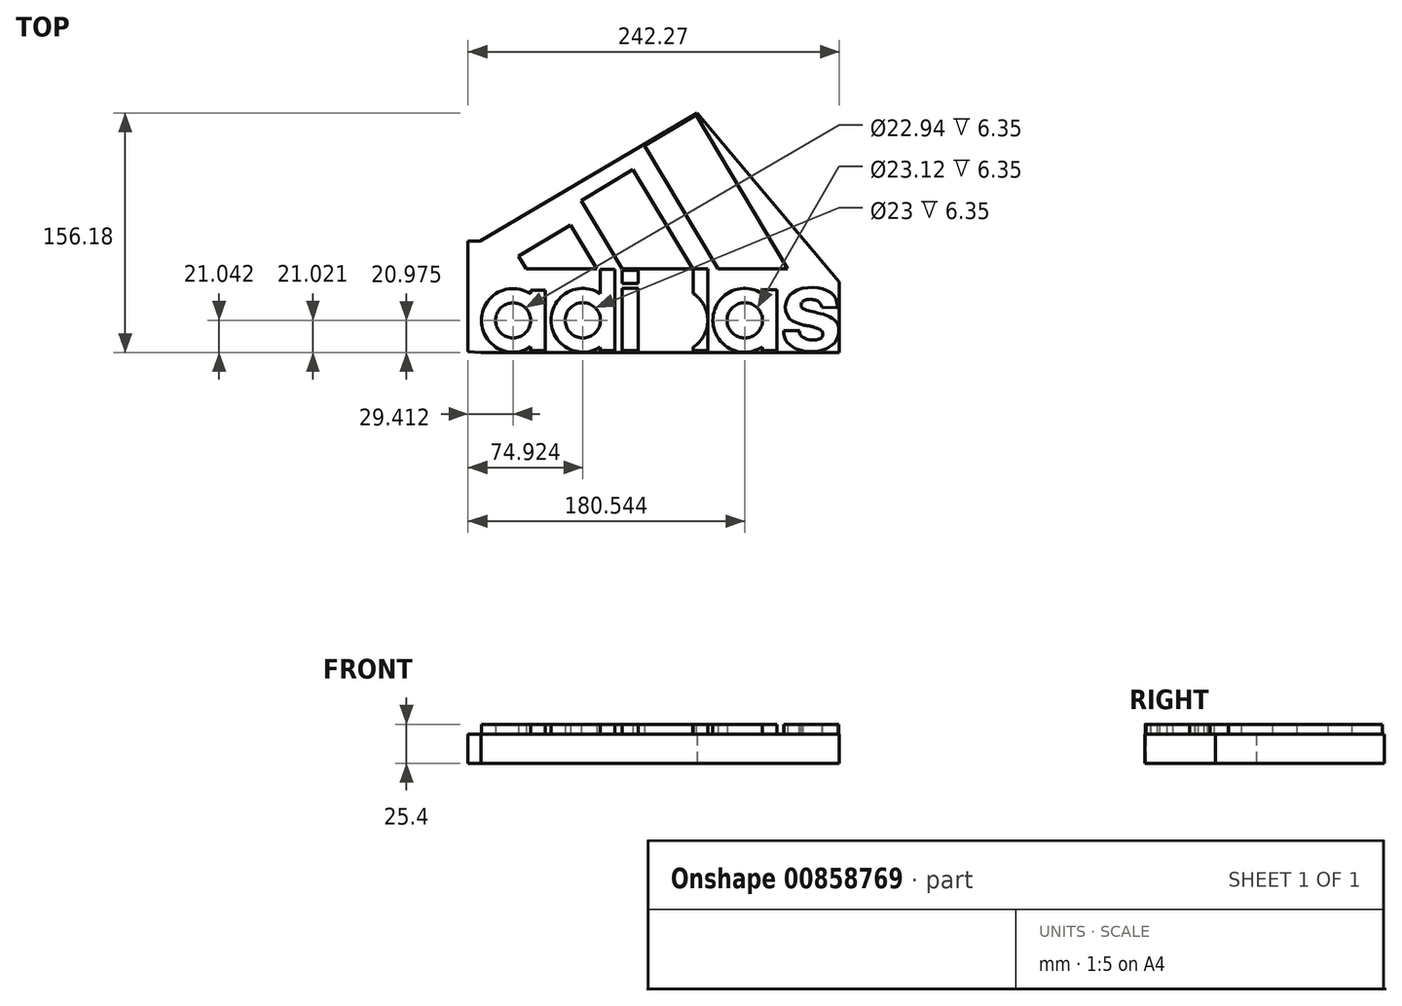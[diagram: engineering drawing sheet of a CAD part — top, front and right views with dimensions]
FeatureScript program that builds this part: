
annotation { "Feature Type Name" : "Feature", "Feature Type Description" : "" }
export const myFeature = defineFeature(function(context is Context, id is Id, definition is map)
    precondition{}
    {
        {
            var Q0;
            Q0=qCreatedBy(makeId("Top.planeOp"),FACE);
            var sketch = newSketch(context, id + "F0", { "sketchPlane" : qUnion([Q0])});
            skLineSegment(sketch, "E0", {"start": v(-91.26, -15.7) * mm, "end": v(-57.48, 4.7) * mm});
            skLineSegment(sketch, "E1", {"start": v(-57.48, 4.7) * mm, "end": v(-40.16, -23.99) * mm});
            skLineSegment(sketch, "E2", {"start": v(-40.16, -23.99) * mm, "end": v(-86.26, -23.99) * mm});
            skLineSegment(sketch, "E3", {"start": v(-86.26, -23.99) * mm, "end": v(-91.26, -15.7) * mm});
            skLineSegment(sketch, "E4", {"start": v(-16.65, 40.75) * mm, "end": v(-50.43, 20.37) * mm});
            skLineSegment(sketch, "E5", {"start": v(-50.43, 20.37) * mm, "end": v(-23.6, -24.1) * mm});
            skLineSegment(sketch, "E6", {"start": v(-23.6, -24.1) * mm, "end": v(22.26, -24.1) * mm});
            skLineSegment(sketch, "E7", {"start": v(22.26, -24.1) * mm, "end": v(-16.65, 40.75) * mm});
            skLineSegment(sketch, "E8", {"start": v(-9.03, 56.5) * mm, "end": v(24.5, 76.51) * mm});
            skLineSegment(sketch, "E9", {"start": v(24.5, 76.51) * mm, "end": v(84.33, -23.8) * mm});
            skLineSegment(sketch, "E10", {"start": v(84.33, -23.8) * mm, "end": v(38.86, -23.8) * mm});
            skLineSegment(sketch, "E11", {"start": v(38.86, -23.8) * mm, "end": v(-9.03, 56.5) * mm});
            skLineSegment(sketch, "E12", {"start": v(-73.9, -37.96) * mm, "end": v(-73.9, -77.28) * mm});
            skLineSegment(sketch, "E13", {"start": v(-73.9, -77.28) * mm, "end": v(-83.4, -77.28) * mm});
            skLineSegment(sketch, "E14", {"start": v(-83.4, -77.28) * mm, "end": v(-83.4, -75.06) * mm});
            skLineSegment(sketch, "E15", {"start": v(-73.9, -37.96) * mm, "end": v(-83.49, -37.96) * mm});
            skLineSegment(sketch, "E16", {"start": v(-83.49, -37.96) * mm, "end": v(-83.49, -39.74) * mm});
            skCircle(sketch, "E17", {"center": v(-94.85, -57.58) * mm, "radius": 11.47 * mm});
            skCircle(sketch, "E18", {"center": v(-94.85, -57.58) * mm, "radius": 20.72 * mm});
            skCircle(sketch, "E19", {"center": v(-49.34, -57.5) * mm, "radius": 11.5 * mm});
            skCircle(sketch, "E20", {"center": v(-49.34, -57.5) * mm, "radius": 20.77 * mm});
            skLineSegment(sketch, "E21", {"start": v(-83.4, -75.06) * mm, "end": v(-83.49, -39.74) * mm});
            skLineSegment(sketch, "E22.bottom", {"start": v(-38.01, -24.27) * mm, "end": v(-28.56, -24.27) * mm});
            skLineSegment(sketch, "E22.top", {"start": v(-38.01, -77.35) * mm, "end": v(-28.56, -77.35) * mm});
            skLineSegment(sketch, "E22.left", {"start": v(-38.01, -24.27) * mm, "end": v(-38.01, -77.35) * mm});
            skLineSegment(sketch, "E22.right", {"start": v(-28.56, -24.27) * mm, "end": v(-28.56, -77.35) * mm});
            skLineSegment(sketch, "E23.bottom", {"start": v(-23.6, -33.52) * mm, "end": v(-13.2, -33.52) * mm});
            skLineSegment(sketch, "E23.top", {"start": v(-23.6, -24.9) * mm, "end": v(-13.2, -24.9) * mm});
            skLineSegment(sketch, "E23.left", {"start": v(-23.6, -33.52) * mm, "end": v(-23.6, -24.9) * mm});
            skLineSegment(sketch, "E23.right", {"start": v(-13.2, -33.52) * mm, "end": v(-13.2, -24.9) * mm});
            skLineSegment(sketch, "E24.bottom", {"start": v(-23.68, -36.53) * mm, "end": v(-13.2, -36.53) * mm});
            skLineSegment(sketch, "E24.top", {"start": v(-23.68, -77.24) * mm, "end": v(-13.2, -77.24) * mm});
            skLineSegment(sketch, "E24.left", {"start": v(-23.68, -36.53) * mm, "end": v(-23.68, -77.24) * mm});
            skLineSegment(sketch, "E24.right", {"start": v(-13.2, -36.53) * mm, "end": v(-13.2, -77.24) * mm});
            skLineSegment(sketch, "E25.bottom", {"start": v(32.16, -77.24) * mm, "end": v(22.7, -77.24) * mm});
            skLineSegment(sketch, "E25.top", {"start": v(32.16, -24.1) * mm, "end": v(22.7, -24.1) * mm});
            skLineSegment(sketch, "E25.left", {"start": v(32.16, -77.24) * mm, "end": v(32.16, -24.1) * mm});
            skLineSegment(sketch, "E25.right", {"start": v(22.7, -77.24) * mm, "end": v(22.7, -24.1) * mm});
            skCircle(sketch, "E26", {"center": v(11.42, -57.53) * mm, "radius": 11.42 * mm});
            skCircle(sketch, "E27", {"center": v(11.42, -57.53) * mm, "radius": 20.73 * mm});
            skCircle(sketch, "E28", {"center": v(56.28, -57.53) * mm, "radius": 11.56 * mm});
            skFitSpline(sketch, "E29", {"points": [v(81.61, -64.38) * mm, v(117.73, -63.94) * mm], "startDerivative": vector(-1.77, -53.7) * mm, "endDerivative": vector(-0.99, 57.2) * mm});
            skFitSpline(sketch, "E30", {"points": [v(117.73, -63.94) * mm, v(93.06, -47.23) * mm], "startDerivative": vector(-0.33, 41.67) * mm, "endDerivative": vector(4.32, 20.27) * mm});
            skLineSegment(sketch, "E31.bottom", {"start": v(67.63, -37.71) * mm, "end": v(77.36, -37.71) * mm});
            skLineSegment(sketch, "E31.top", {"start": v(67.63, -77.26) * mm, "end": v(77.36, -77.26) * mm});
            skLineSegment(sketch, "E31.left", {"start": v(67.63, -37.71) * mm, "end": v(67.63, -77.26) * mm});
            skLineSegment(sketch, "E31.right", {"start": v(77.36, -37.71) * mm, "end": v(77.36, -77.26) * mm});
            skCircle(sketch, "E32", {"center": v(56.28, -57.53) * mm, "radius": 20.8 * mm});
            skFitSpline(sketch, "E33", {"points": [v(93.06, -47.23) * mm, v(106.38, -49.16) * mm], "startDerivative": vector(3.38, 16.63) * mm, "endDerivative": vector(-1.1, -17.88) * mm});
            skLineSegment(sketch, "E34", {"start": v(92.14, -64.35) * mm, "end": v(81.61, -64.38) * mm});
            skLineSegment(sketch, "E35", {"start": v(116.62, -49.23) * mm, "end": v(106.38, -49.16) * mm});
            skPoint(sketch, "E36.1.internal.snap0", {"position": v(111.5, -49.2) * mm});
            skFitSpline(sketch, "E37", {"points": [v(92.14, -64.35) * mm, v(106.58, -64.35) * mm], "startDerivative": vector(-5.97, -20.58) * mm, "endDerivative": vector(-12.92, 27.57) * mm});
            skFitSpline(sketch, "E38", {"points": [v(106.58, -64.35) * mm, v(94, -60.6) * mm], "startDerivative": vector(-5.75, 4.6) * mm, "endDerivative": vector(-16.11, 1.37) * mm});
            skFitSpline(sketch, "E39", {"points": [v(94, -60.6) * mm, v(87.01, -57.76) * mm, v(84.52, -55.12) * mm, v(82.67, -49.71) * mm, v(83.67, -44.8) * mm, v(85.52, -41.38) * mm, v(89.93, -38.03) * mm, v(97.55, -36.18) * mm, v(104.32, -36.54) * mm, v(110.16, -38.25) * mm, v(114.15, -41.3) * mm, v(115.93, -44.37) * mm, v(116.64, -48.36) * mm, v(116.71, -49.23) * mm, v(116.62, -49.23) * mm], "startDerivative": vector(-85.4, 29.14) * mm, "endDerivative": vector(-29.4, 5.26) * mm});
            skSolve(sketch);
        }
        {
            var Q0;
            Q0=qCreatedBy(makeId("Top.planeOp"),FACE);
            var sketch = newSketch(context, id + "F1", { "sketchPlane" : qUnion([Q0])});
            skLineSegment(sketch, "E40", {"start": v(118, -70.14) * mm, "end": v(16.35, 70.24) * mm});
            skLineSegment(sketch, "E41", {"start": v(16.35, 70.24) * mm, "end": v(-115.79, -59.54) * mm});
            skLineSegment(sketch, "E42", {"start": v(-115.79, -59.54) * mm, "end": v(118, -70.14) * mm});
            skLineSegment(sketch, "E43", {"start": v(-115.79, -59.54) * mm, "end": v(-115.79, -78.55) * mm});
            skLineSegment(sketch, "E44", {"start": v(-115.79, -78.55) * mm, "end": v(118, -78.55) * mm});
            skLineSegment(sketch, "E45", {"start": v(118, -78.55) * mm, "end": v(118, -70.14) * mm});
            skLineSegment(sketch, "E46", {"start": v(118, -70.14) * mm, "end": v(118, -32.43) * mm});
            skLineSegment(sketch, "E47", {"start": v(118, -32.43) * mm, "end": v(25.04, 77.63) * mm});
            skLineSegment(sketch, "E48", {"start": v(25.04, 77.63) * mm, "end": v(-116.56, -5.85) * mm});
            skLineSegment(sketch, "E49", {"start": v(-116.56, -5.85) * mm, "end": v(-115.79, -59.54) * mm});
            skLineSegment(sketch, "E50", {"start": v(-116.56, -5.85) * mm, "end": v(-124.26, -5.96) * mm});
            skLineSegment(sketch, "E51", {"start": v(-124.26, -5.96) * mm, "end": v(-124.26, -77.9) * mm});
            skLineSegment(sketch, "E52", {"start": v(-124.26, -77.9) * mm, "end": v(-115.79, -78.55) * mm});
            skSolve(sketch);
        }
        {
            var Q0;
            Q0=makeQuery(id+"F0.imprint","IMPRINT",FACE,{"disambiguationData":[TD([[makeQuery(id+"F0.imprint","IMPRINT",EDGE,{"derivedFrom":sQuery(id+"F0.wireOp",EDGE,"E4")}),1.0]])]});
            var Q1;
            Q1=makeQuery(id+"F0.imprint","IMPRINT",FACE,{"disambiguationData":[TD([[makeQuery(id+"F0.imprint","IMPRINT",EDGE,{"derivedFrom":sQuery(id+"F0.wireOp",EDGE,"E8")}),-1.0]])]});
            var Q2;
            Q2=makeQuery(id+"F0.imprint","IMPRINT",FACE,{"disambiguationData":[TD([[makeQuery(id+"F0.imprint","IMPRINT",EDGE,{"derivedFrom":sQuery(id+"F0.wireOp",EDGE,"E0")}),-1.0]])]});
            var Q3;
            {var subQ0=sQuery(id+"F0.wireOp",EDGE,"E22.left");var subQ1=sQuery(id+"F0.wireOp",EDGE,"E19");var subQ2=makeQuery(id+"F0.imprint","INTERSECT",VERTEX,{"disambiguationData":[OD(0.0)],"derivedFrom":[subQ1,subQ0]});Q3=makeQuery(id+"F0.imprint","IMPRINT",FACE,{"disambiguationData":[TD([[makeQuery(id+"F0.imprint","IMPRINT",EDGE,{"disambiguationData":[TD([[subQ2,-1.0]])],"derivedFrom":subQ1}),-1.0]])]});}
            var Q4;
            {var subQ0=sQuery(id+"F0.wireOp",EDGE,"E22.left");var subQ1=sQuery(id+"F0.wireOp",EDGE,"E19");var subQ2=makeQuery(id+"F0.imprint","INTERSECT",VERTEX,{"disambiguationData":[OD(0.0)],"derivedFrom":[subQ1,subQ0]});Q4=makeQuery(id+"F0.imprint","IMPRINT",FACE,{"disambiguationData":[TD([[makeQuery(id+"F0.imprint","IMPRINT",EDGE,{"disambiguationData":[TD([[subQ2,1.0]])],"derivedFrom":subQ1}),-1.0]])]});}
            var Q5;
            {var subQ1=sQuery(id+"F0.wireOp",EDGE,"E22.bottom");Q5=makeQuery(id+"F0.imprint","IMPRINT",FACE,{"disambiguationData":[TD([[makeQuery(id+"F0.imprint","IMPRINT",EDGE,{"derivedFrom":subQ1}),-1.0]])]});}
            var Q6;
            {var subQ0=sQuery(id+"F0.wireOp",EDGE,"E21");var subQ1=sQuery(id+"F0.wireOp",EDGE,"E17");var subQ2=makeQuery(id+"F0.imprint","INTERSECT",VERTEX,{"disambiguationData":[OD(0.0)],"derivedFrom":[subQ1,subQ0]});Q6=makeQuery(id+"F0.imprint","IMPRINT",FACE,{"disambiguationData":[TD([[makeQuery(id+"F0.imprint","IMPRINT",EDGE,{"disambiguationData":[TD([[subQ2,-1.0]])],"derivedFrom":subQ1}),-1.0]])]});}
            var Q7;
            Q7=makeQuery(id+"F0.imprint","IMPRINT",FACE,{"disambiguationData":[TD([[makeQuery(id+"F0.imprint","IMPRINT",EDGE,{"derivedFrom":sQuery(id+"F0.wireOp",EDGE,"E12")}),-1.0]])]});
            var Q8;
            {var subQ0=sQuery(id+"F0.wireOp",EDGE,"E21");var subQ1=sQuery(id+"F0.wireOp",EDGE,"E17");var subQ2=makeQuery(id+"F0.imprint","INTERSECT",VERTEX,{"disambiguationData":[OD(0.0)],"derivedFrom":[subQ1,subQ0]});Q8=makeQuery(id+"F0.imprint","IMPRINT",FACE,{"disambiguationData":[TD([[makeQuery(id+"F0.imprint","IMPRINT",EDGE,{"disambiguationData":[TD([[subQ2,1.0]])],"derivedFrom":subQ1}),-1.0]])]});}
            var Q9;
            Q9=makeQuery(id+"F0.imprint","IMPRINT",FACE,{"disambiguationData":[TD([[makeQuery(id+"F0.imprint","IMPRINT",EDGE,{"derivedFrom":sQuery(id+"F0.wireOp",EDGE,"E24.bottom")}),-1.0]])]});
            var Q10;
            Q10=makeQuery(id+"F0.imprint","IMPRINT",FACE,{"disambiguationData":[TD([[makeQuery(id+"F0.imprint","IMPRINT",EDGE,{"derivedFrom":sQuery(id+"F0.wireOp",EDGE,"E23.bottom")}),1.0]])]});
            var Q11;
            {var subQ0=sQuery(id+"F0.wireOp",EDGE,"E27");var subQ1=sQuery(id+"F0.wireOp",EDGE,"E25.right");var subQ2=makeQuery(id+"F0.imprint","INTERSECT",VERTEX,{"disambiguationData":[OD(0.0)],"derivedFrom":[subQ1,subQ0]});Q11=makeQuery(id+"F0.imprint","IMPRINT",FACE,{"disambiguationData":[TD([[makeQuery(id+"F0.imprint","IMPRINT",EDGE,{"disambiguationData":[TD([[subQ2,-1.0]])],"derivedFrom":subQ1}),1.0]])]});}
            var Q12;
            {var subQ0=sQuery(id+"F0.wireOp",EDGE,"E27");var subQ1=sQuery(id+"F0.wireOp",EDGE,"E25.right");var subQ2=makeQuery(id+"F0.imprint","INTERSECT",VERTEX,{"disambiguationData":[OD(0.0)],"derivedFrom":[subQ1,subQ0]});Q12=makeQuery(id+"F0.imprint","IMPRINT",FACE,{"disambiguationData":[TD([[makeQuery(id+"F0.imprint","IMPRINT",EDGE,{"disambiguationData":[TD([[subQ2,-1.0]])],"derivedFrom":subQ1}),-1.0]])]});}
            var Q13;
            {var subQ1=sQuery(id+"F0.wireOp",EDGE,"E25.bottom");Q13=makeQuery(id+"F0.imprint","IMPRINT",FACE,{"disambiguationData":[TD([[makeQuery(id+"F0.imprint","IMPRINT",EDGE,{"derivedFrom":subQ1}),-1.0]])]});}
            var Q14;
            {var subQ0=sQuery(id+"F0.wireOp",EDGE,"E31.left");var subQ1=sQuery(id+"F0.wireOp",EDGE,"E28");var subQ2=makeQuery(id+"F0.imprint","INTERSECT",VERTEX,{"disambiguationData":[OD(0.0)],"derivedFrom":[subQ1,subQ0]});Q14=makeQuery(id+"F0.imprint","IMPRINT",FACE,{"disambiguationData":[TD([[makeQuery(id+"F0.imprint","IMPRINT",EDGE,{"disambiguationData":[TD([[subQ2,-1.0]])],"derivedFrom":subQ1}),-1.0]])]});}
            var Q15;
            {var subQ0=sQuery(id+"F0.wireOp",EDGE,"E31.left");var subQ1=sQuery(id+"F0.wireOp",EDGE,"E28");var subQ2=makeQuery(id+"F0.imprint","INTERSECT",VERTEX,{"disambiguationData":[OD(0.0)],"derivedFrom":[subQ1,subQ0]});Q15=makeQuery(id+"F0.imprint","IMPRINT",FACE,{"disambiguationData":[TD([[makeQuery(id+"F0.imprint","IMPRINT",EDGE,{"disambiguationData":[TD([[subQ2,1.0]])],"derivedFrom":subQ1}),-1.0]])]});}
            var Q16;
            {var subQ1=sQuery(id+"F0.wireOp",EDGE,"E31.bottom");Q16=makeQuery(id+"F0.imprint","IMPRINT",FACE,{"disambiguationData":[TD([[makeQuery(id+"F0.imprint","IMPRINT",EDGE,{"derivedFrom":subQ1}),-1.0]])]});}
            var Q17;
            Q17=makeQuery(id+"F0.imprint","IMPRINT",FACE,{"disambiguationData":[TD([[makeQuery(id+"F0.imprint","IMPRINT",EDGE,{"derivedFrom":sQuery(id+"F0.wireOp",EDGE,"E29")}),1.0]])]});
            extrude(context, id + "F2", {"entities" : qUnion([Q0, Q1, Q2, Q3, Q4, Q5, Q6, Q7, Q8, Q9, Q10, Q11, Q12, Q13, Q14, Q15, Q16, Q17]), "depth" : 25.4 * mm, "offsetDistance" : 25.4 * mm});
        }
        {
            var Q0;
            Q0=makeQuery(id+"F1.imprint","IMPRINT",FACE,{"disambiguationData":[TD([[makeQuery(id+"F1.imprint","IMPRINT",EDGE,{"derivedFrom":sQuery(id+"F1.wireOp",EDGE,"E40")}),-1.0]])]});
            var Q1;
            Q1=makeQuery(id+"F1.imprint","IMPRINT",FACE,{"disambiguationData":[TD([[makeQuery(id+"F1.imprint","IMPRINT",EDGE,{"derivedFrom":sQuery(id+"F1.wireOp",EDGE,"E43")}),-1.0]])]});
            var Q2;
            Q2=makeQuery(id+"F1.imprint","IMPRINT",FACE,{"disambiguationData":[TD([[makeQuery(id+"F1.imprint","IMPRINT",EDGE,{"derivedFrom":sQuery(id+"F1.wireOp",EDGE,"E42")}),-1.0]])]});
            var Q3;
            Q3=makeQuery(id+"F1.imprint","IMPRINT",FACE,{"disambiguationData":[TD([[makeQuery(id+"F1.imprint","IMPRINT",EDGE,{"derivedFrom":sQuery(id+"F1.wireOp",EDGE,"E40")}),1.0]])]});
            extrude(context, id + "F3", {"entities" : qUnion([Q0, Q1, Q2, Q3]), "operationType" : NewBodyOperationType.ADD, "depth" : 19.05 * mm, "offsetDistance" : 25.4 * mm});
        }
    });
